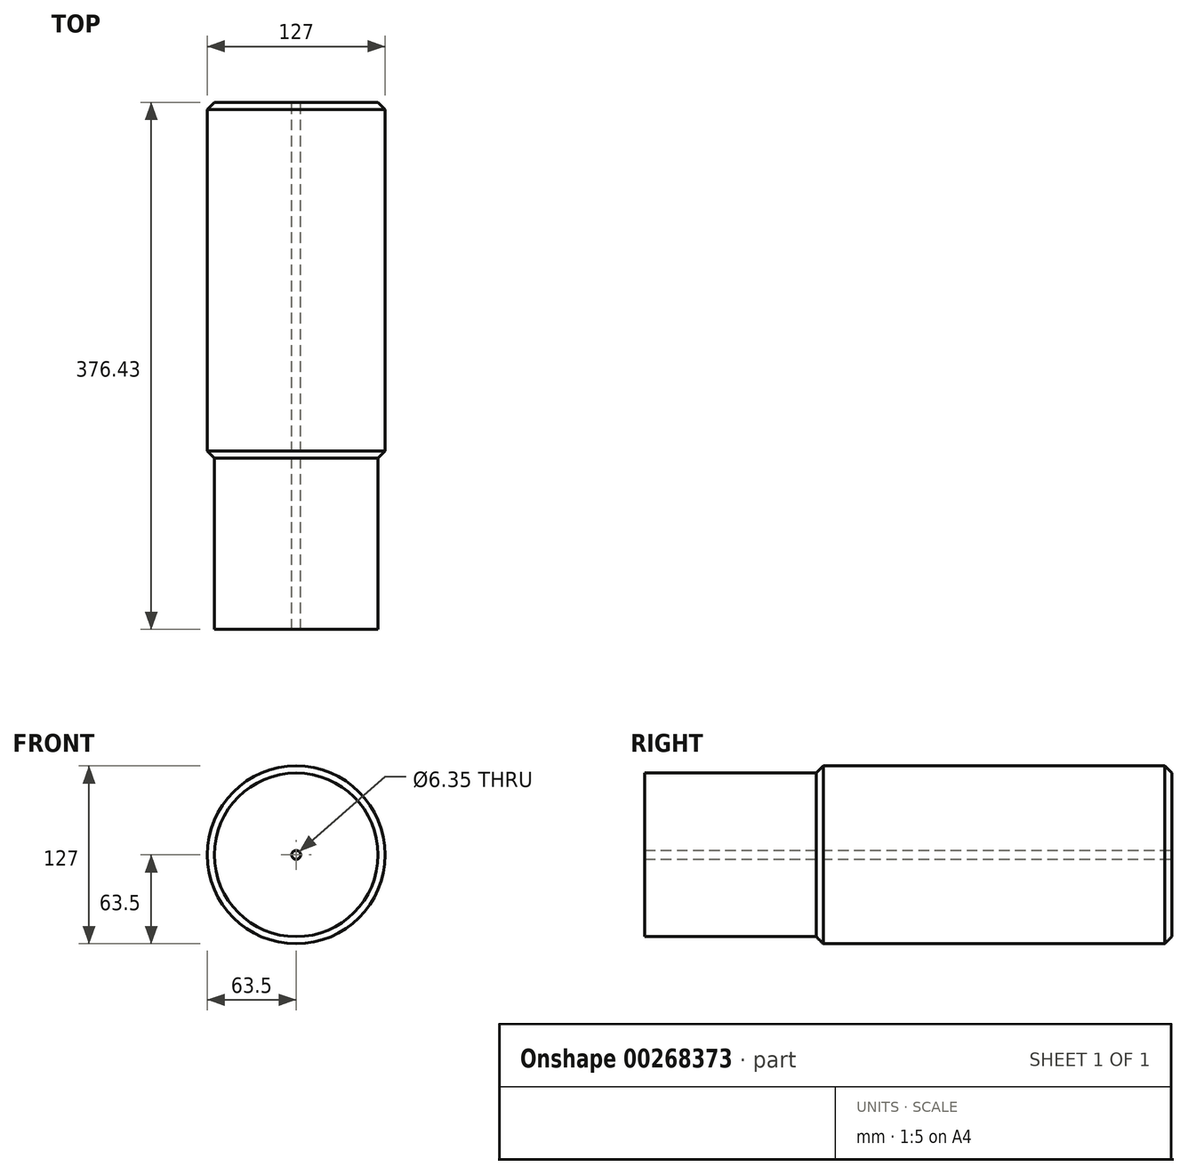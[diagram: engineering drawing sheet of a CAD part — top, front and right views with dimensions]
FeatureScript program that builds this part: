
annotation { "Feature Type Name" : "Feature", "Feature Type Description" : "" }
export const myFeature = defineFeature(function(context is Context, id is Id, definition is map)
    precondition{}
    {
        {
            var Q0;
            Q0=qCreatedBy(makeId("Front.planeOp"),FACE);
            var sketch = newSketch(context, id + "F0", { "sketchPlane" : qUnion([Q0])});
            skCircle(sketch, "E0", {"center": v(0, 0) * mm, "radius": 63.5 * mm});
            skSolve(sketch);
        }
        {
            var Q0;
            Q0=makeQuery(id+"F0.imprint","IMPRINT",FACE,{"disambiguationData":[TD([[makeQuery(id+"F0.imprint","IMPRINT",EDGE,{"derivedFrom":sQuery(id+"F0.wireOp",EDGE,"E0")}),1.0]])]});
            extrude(context, id + "F1", {"entities" : qUnion([Q0]), "oppositeDirection" : true, "depth" : 254 * mm});
        }
        {
            var Q0;
            Q0=makeQuery(id+"F1.opExtrude","SWEPT_FACE",FACE,{"disambiguationData":[OSD([sQuery(id+"F0.wireOp",EDGE,"E0")])]});
            chamfer(context, id + "F2", {"entities" : qUnion([Q0]), "chamferType" : ChamferType.TWO_OFFSETS, "width1" : 5.08 * mm, "oppositeDirection" : false, "width2" : 5.08 * mm});
        }
        {
            var Q0;
            Q0=makeQuery(id+"F1.opExtrude","CAP_FACE",FACE,{"disambiguationData":[OSD([sQuery(id+"F0.wireOp",EDGE,"E0")])],"isStart":false});
            var sketch = newSketch(context, id + "F3", { "sketchPlane" : qUnion([Q0])});
            skCircle(sketch, "E1", {"center": v(0, 0) * mm, "radius": 27.26 * mm});
            skSolve(sketch);
        }
        {
            var Q0;
            Q0=sQuery(id+"F3.wireOp",VERTEX,"E1.center");
            var Q1;
            Q1=makeQuery(id+"F1.opExtrude","SWEPT_BODY",BODY,{"disambiguationData":[OSD([sQuery(id+"F0.wireOp",EDGE,"E0")])]});
            hole(context, id + "F4", {"style" : HoleStyle.SIMPLE, "endStyle" : HoleEndStyle.THROUGH, "holeDiameter" : 6.35 * mm, "majorDiameter" : 6.35 * mm, "isTappedThrough" : true, "tappedDepth" : 12.7 * mm, "tapClearance" : 3, "locations" : qUnion([Q0]), "scope" : qUnion([Q1])});
        }
        {
            var Q0;
            Q0=makeQuery(id+"F1.opExtrude","CAP_FACE",FACE,{"disambiguationData":[OSD([sQuery(id+"F0.wireOp",EDGE,"E0")])],"isStart":true});
            extrude(context, id + "F5", {"entities" : qUnion([Q0]), "operationType" : NewBodyOperationType.ADD, "depth" : 122.43 * mm, "offsetDistance" : 25.4 * mm});
        }
    });
